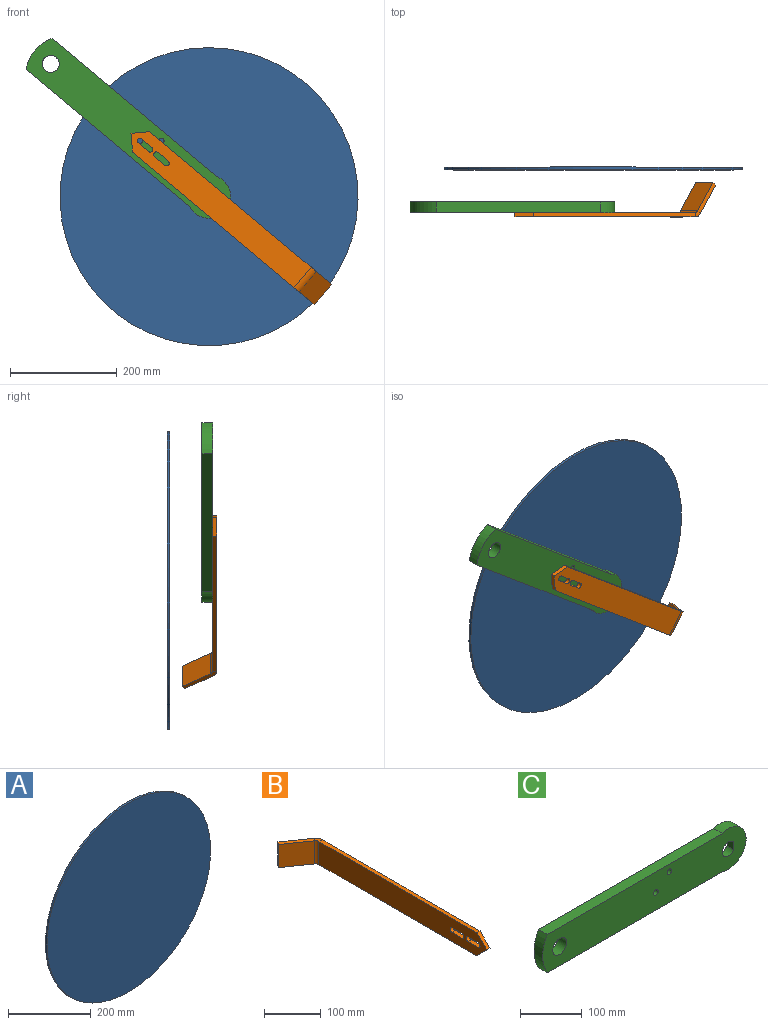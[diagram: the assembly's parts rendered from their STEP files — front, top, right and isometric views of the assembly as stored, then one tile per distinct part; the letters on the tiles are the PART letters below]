
ASSEMBLY  parts=3 mates=2
PART A: 3 faces, bbox 558.8x5x558.8 mm
  f0: cylinder r=279.4mm len=558.8mm, axis (0,-1,0), area 8777.6mm2, adj f1,f2
  f1: plane 558.8x558.8mm, normal (0,1,0), area 245246.4mm2, adj f0
  f2: plane 558.8x558.8mm, normal (0,-1,0), area 245246.4mm2, adj f0
PART B: 23 faces, bbox 64.6x470x50 mm
  f0: plane 25x8mm, normal (0,0,-1), area 200mm2, adj f1,f11,f12,f13
  f1: cylinder r=5mm len=10mm, axis (1,0,0), area 125.7mm2, adj f0,f2,f12,f13
  f2: plane 25x8mm, normal (0,0,1), area 200mm2, adj f1,f11,f12,f13
  f3: plane 25x8mm, normal (0,0,1), area 200mm2, adj f4,f10,f12,f13
  f4: cylinder r=5mm len=10mm, axis (1,0,0), area 125.7mm2, adj f3,f5,f12,f13
  f5: plane 25x8mm, normal (0,0,-1), area 200mm2, adj f4,f10,f12,f13
  f6: plane 25x25mm, normal (0,-0.71,-0.71), area 282.8mm2, adj f7,f9,f12,f13
  f7: plane 394.66x8mm, normal (0,0,-1), area 3157.3mm2, adj f6,f12,f13,f20
  f8: plane 394.66x8mm, normal (0,0,1), area 3157.3mm2, adj f9,f12,f13,f19
  f9: plane 25x25mm, normal (0,-0.71,0.71), area 282.8mm2, adj f6,f8,f12,f13
  f10: cylinder r=5mm len=10mm, axis (1,0,0), area 125.7mm2, adj f3,f5,f12,f13
  f11: cylinder r=5mm len=10mm, axis (1,0,0), area 125.7mm2, adj f0,f2,f12,f13
  f12: plane 419.66x50mm, normal (1,0,0), area 19700.8mm2, adj f0,f1,f2,f3,f4,f5,f6,f7
  f13: plane 419.66x50mm, normal (-1,0,0), area 19700.8mm2, adj f0,f1,f2,f3,f4,f5,f6,f7
  f14: plane 57.77x43.79mm, normal (0,0,-1), area 519.3mm2, adj f15,f17,f18,f20
  f15: plane 50x6.55mm, normal (-0.82,0.57,0), area 400mm2, adj f14,f16,f17,f18
  f16: plane 57.77x43.79mm, normal (0,0,1), area 519.3mm2, adj f15,f17,f18,f19
  f17: plane 53.18x50mm, normal (0.57,0.82,0), area 3245.9mm2, adj f14,f15,f16,f21
  f18: plane 53.18x50mm, normal (-0.57,-0.82,0), area 3245.9mm2, adj f14,f15,f16,f22
  f19: plane 13.11x11.41mm, normal (0,0,1), area 92.2mm2, adj f8,f16,f21,f22
  f20: plane 13.11x11.41mm, normal (0,0,-1), area 92.2mm2, adj f7,f14,f21,f22
  f21: cylinder r=16mm len=50mm, axis (0,0,1), area 767.9mm2, adj f12,f17,f19,f20
  f22: cylinder r=8mm len=50mm, axis (0,0,1), area 384mm2, adj f13,f18,f19,f20
PART C: 13 faces, bbox 467.1x20x81 mm
  f0: plane 401.99x20mm, normal (0,0,-1), area 8039.8mm2, adj f2,f3,f7,f8
  f1: plane 401.99x20mm, normal (0,0,1), area 8039.8mm2, adj f2,f3,f7,f8
  f2: plane 467.1x81mm, normal (0,1,0), area 32454.7mm2, adj f0,f1,f6,f7,f8,f9,f10,f11
  f3: plane 467.1x81mm, normal (0,-1,0), area 33211.2mm2, adj f0,f1,f4,f5,f6,f7,f8,f9
  f4: plane 15x14.42mm, normal (-1,0,0), area 216.3mm2, adj f3,f5,f12
  f5: cylinder r=14mm len=28mm, axis (0,-1,0), area 1092.2mm2, adj f3,f4,f12
  f6: cylinder r=16mm len=32mm, axis (0,-1,0), area 2010.6mm2, adj f2,f3
  f7: cylinder r=40.5mm len=81mm, axis (0,-1,0), area 3116.9mm2, adj f0,f1,f2,f3
  f8: cylinder r=73.41mm len=76mm, axis (0,-1,0), area 1597.7mm2, adj f0,f1,f2,f3
  f9: cylinder r=5.25mm len=20mm, axis (0,-1,0), area 659.7mm2, adj f2,f3
  f10: cylinder r=5.25mm len=20mm, axis (0,-1,0), area 659.7mm2, adj f2,f3
  f11: cylinder r=20.75mm len=41.5mm, axis (0,1,0), area 651.9mm2, adj f2,f12
  f12: plane 41.5x41.5mm, normal (0,1,0), area 756.4mm2, adj f4,f5,f11
PLACE A rot(axis=(0,1,0),40deg) t=(-382.67,299.44,99.29)mm
PLACE B rot(axis=(-0.32,0.32,-0.89),96.7deg) t=(-270.18,239.51,17.84)mm
PLACE C rot(axis=(0,1,0),40deg) t=(-382.67,239.44,99.29)mm fixed
MATE fastened A.f0 <-> C.f11  axis (0,-1,0) through (-307.77,327.51,86.05)mm
MATE revolute C.f10 <-> B.f4  axis (0,-1,0) through (-437.22,247.51,190.65)mm
